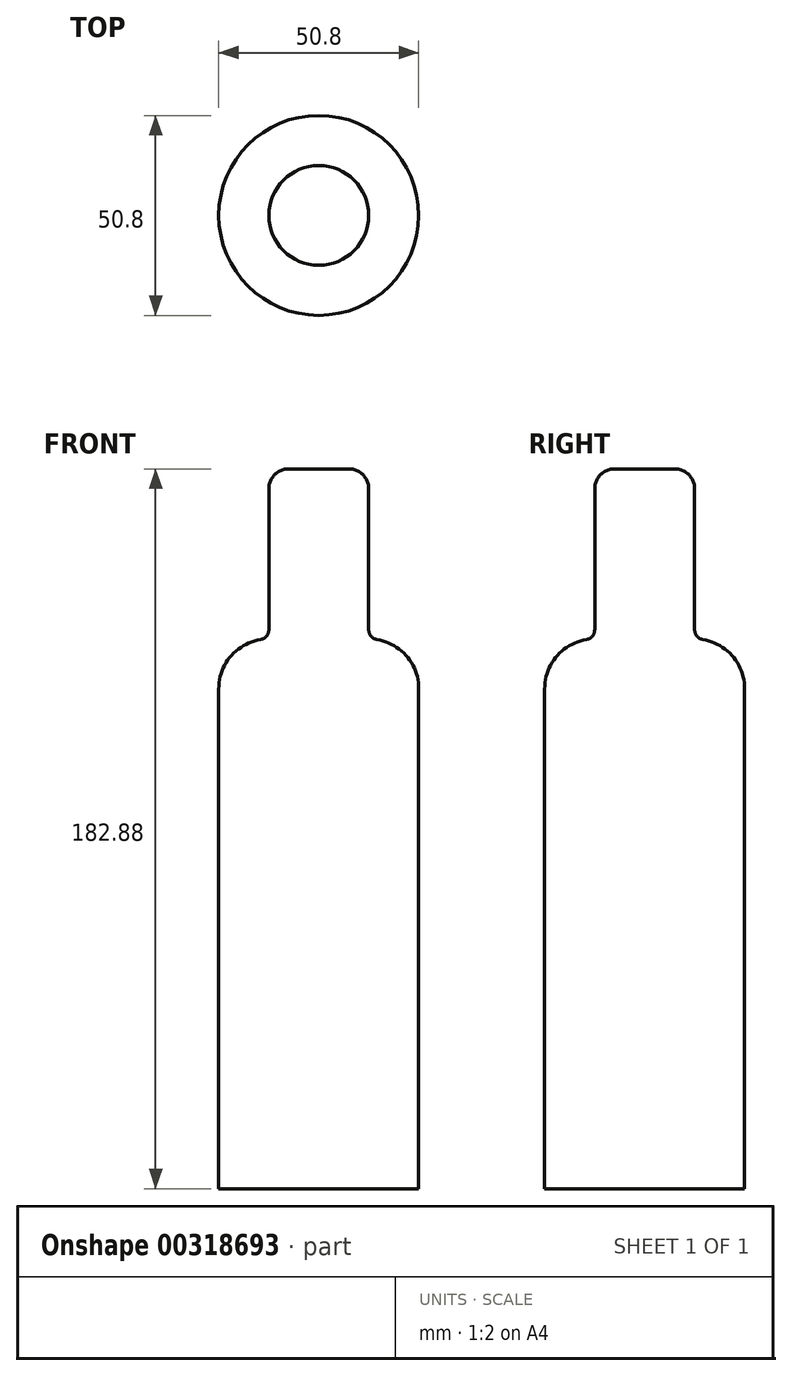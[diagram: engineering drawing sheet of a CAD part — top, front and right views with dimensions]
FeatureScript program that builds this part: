
annotation { "Feature Type Name" : "Feature", "Feature Type Description" : "" }
export const myFeature = defineFeature(function(context is Context, id is Id, definition is map)
    precondition{}
    {
        {
            var Q0;
            Q0=qCreatedBy(makeId("Top.planeOp"),FACE);
            var sketch = newSketch(context, id + "F0", { "sketchPlane" : qUnion([Q0])});
            skCircle(sketch, "E0", {"center": v(0, 0) * mm, "radius": 25.4 * mm});
            skSolve(sketch);
        }
        {
            var Q0;
            Q0 = qSketchRegion(id + "F0", true);
            extrude(context, id + "F1", {"entities" : qUnion([Q0]), "endBound" : BoundingType.SYMMETRIC, "depth" : 139.7 * mm});
        }
        {
            var Q0;
            Q0=makeQuery(id+"F1.opExtrude","CAP_EDGE",EDGE,{"disambiguationData":[OSD([sQuery(id+"F0.wireOp",EDGE,"E0")])],"isStart":false});
            fillet(context, id + "F2", {"entities" : qUnion([Q0]), "radius" : 12.7 * mm, "tangentPropagation" : true, "allowEdgeOverflow" : false});
        }
        {
            var Q0;
            Q0=makeQuery(id+"F1.opExtrude","CAP_FACE",FACE,{"disambiguationData":[OSD([sQuery(id+"F0.wireOp",EDGE,"E0")])],"isStart":false});
            var sketch = newSketch(context, id + "F3", { "sketchPlane" : qUnion([Q0])});
            skCircle(sketch, "E1", {"center": v(0, 0) * mm, "radius": 12.7 * mm});
            skSolve(sketch);
        }
        {
            var Q0;
            Q0 = qSketchRegion(id + "F3", true);
            var Q1;
            Q1=makeQuery(id+"F2.opFillet","BLEND_FACE",FACE,{"disambiguationData":[OSD([sQuery(id+"F0.wireOp",EDGE,"E0")])]});
            extrude(context, id + "F4", {"entities" : qUnion([Q0]), "operationType" : NewBodyOperationType.ADD, "endBoundEntityFace" : qUnion([Q1]), "depth" : 43.18 * mm});
        }
        {
            var Q0;
            Q0=makeQuery(id+"F4.opExtrude","CAP_EDGE",EDGE,{"disambiguationData":[OSD([sQuery(id+"F3.wireOp",EDGE,"E1")])],"isStart":false});
            fillet(context, id + "F5", {"entities" : qUnion([Q0]), "radius" : 5.08 * mm, "tangentPropagation" : true, "allowEdgeOverflow" : false});
        }
        {
            var Q0;
            {var subQ0=sQuery(id+"F0.wireOp",EDGE,"E0");Q0=makeQuery(id+"F4.boolean.opBoolean","MERGE",EDGE,{"derivedFrom":[makeQuery(id+"F2.opFillet","BLEND_EDGE",EDGE,{"blendedFrom":[makeQuery(id+"F1.opExtrude","CAP_EDGE",EDGE,{"disambiguationData":[OSD([subQ0])],"isStart":false}),makeQuery(id+"F1.opExtrude","CAP_FACE",FACE,{"disambiguationData":[OSD([subQ0])],"isStart":false})],"blendedInto":[makeQuery(id+"F1.opExtrude","CAP_FACE",FACE,{"disambiguationData":[OSD([subQ0])],"isStart":false})]}),makeQuery(id+"F4.opExtrude","CAP_EDGE",EDGE,{"disambiguationData":[OSD([sQuery(id+"F3.wireOp",EDGE,"E1")])],"isStart":true})]});}
            fillet(context, id + "F6", {"entities" : qUnion([Q0]), "radius" : 2.54 * mm, "allowEdgeOverflow" : false});
        }
    });
